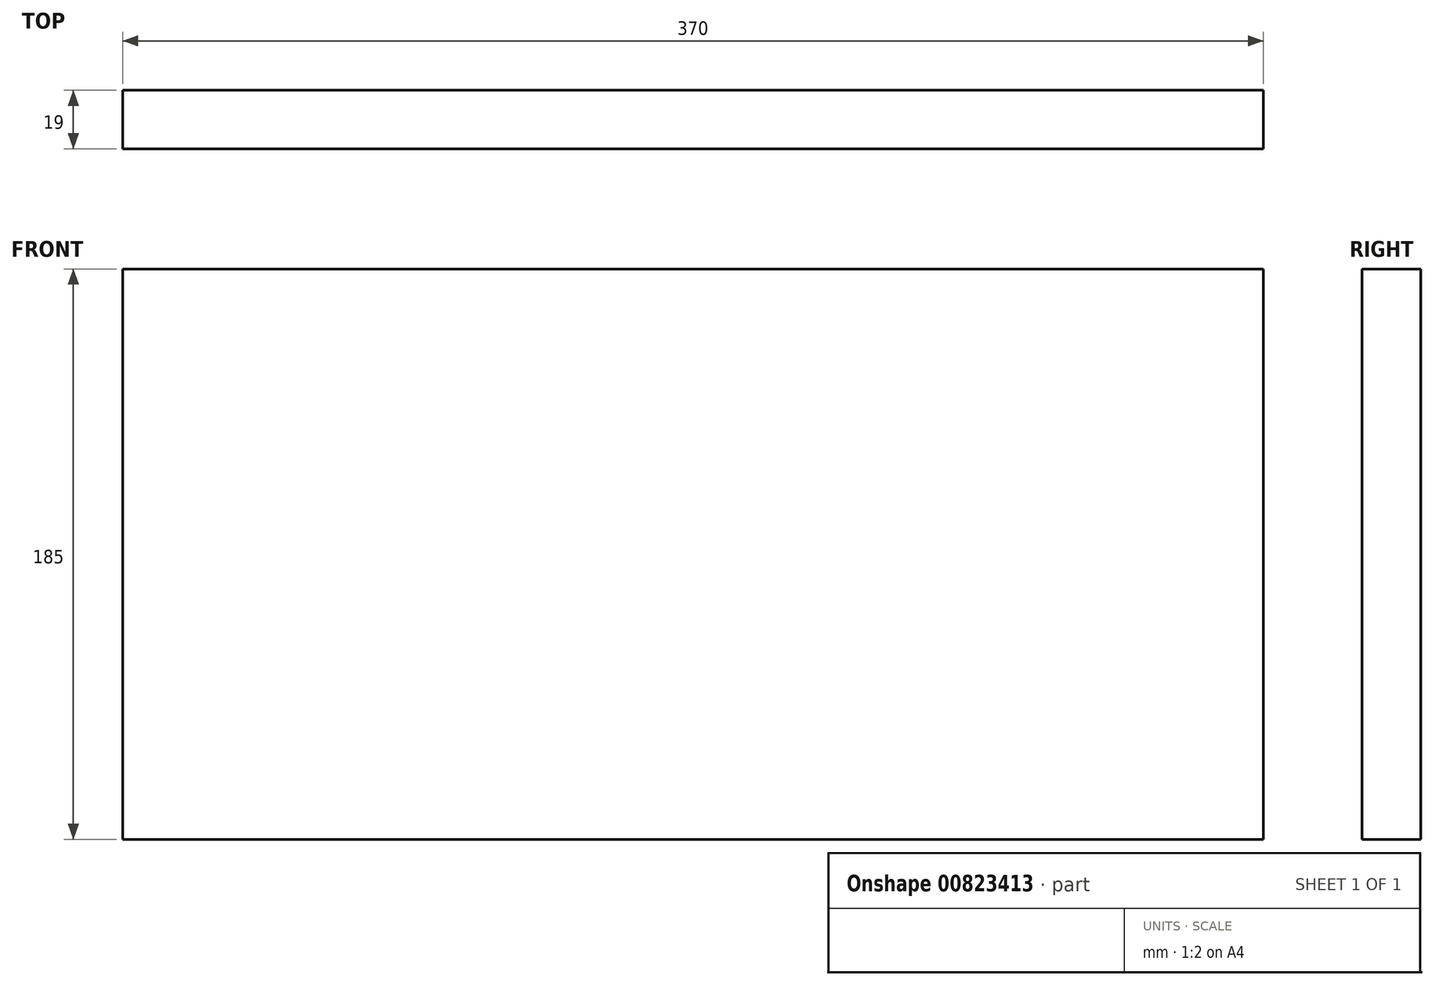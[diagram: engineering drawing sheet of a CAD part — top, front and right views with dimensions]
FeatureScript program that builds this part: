
annotation { "Feature Type Name" : "Feature", "Feature Type Description" : "" }
export const myFeature = defineFeature(function(context is Context, id is Id, definition is map)
    precondition{}
    {
        {
            var Q0;
            Q0=qCreatedBy(makeId("Front.planeOp"),FACE);
            var sketch = newSketch(context, id + "F0", { "sketchPlane" : qUnion([Q0])});
            skLineSegment(sketch, "E0.bottom", {"start": v(185, 92.5) * mm, "end": v(-185, 92.5) * mm});
            skLineSegment(sketch, "E0.top", {"start": v(185, -92.5) * mm, "end": v(-185, -92.5) * mm});
            skLineSegment(sketch, "E0.left", {"start": v(185, 92.5) * mm, "end": v(185, -92.5) * mm});
            skLineSegment(sketch, "E0.right", {"start": v(-185, 92.5) * mm, "end": v(-185, -92.5) * mm});
            skPoint(sketch, "E0.middle", {"position": v(0, 0) * mm});
            skSolve(sketch);
        }
        {
            var Q0;
            Q0 = qSketchRegion(id + "F0", true);
            extrude(context, id + "F1", {"entities" : qUnion([Q0]), "depth" : 19 * mm, "offsetDistance" : 25 * mm});
        }
    });
